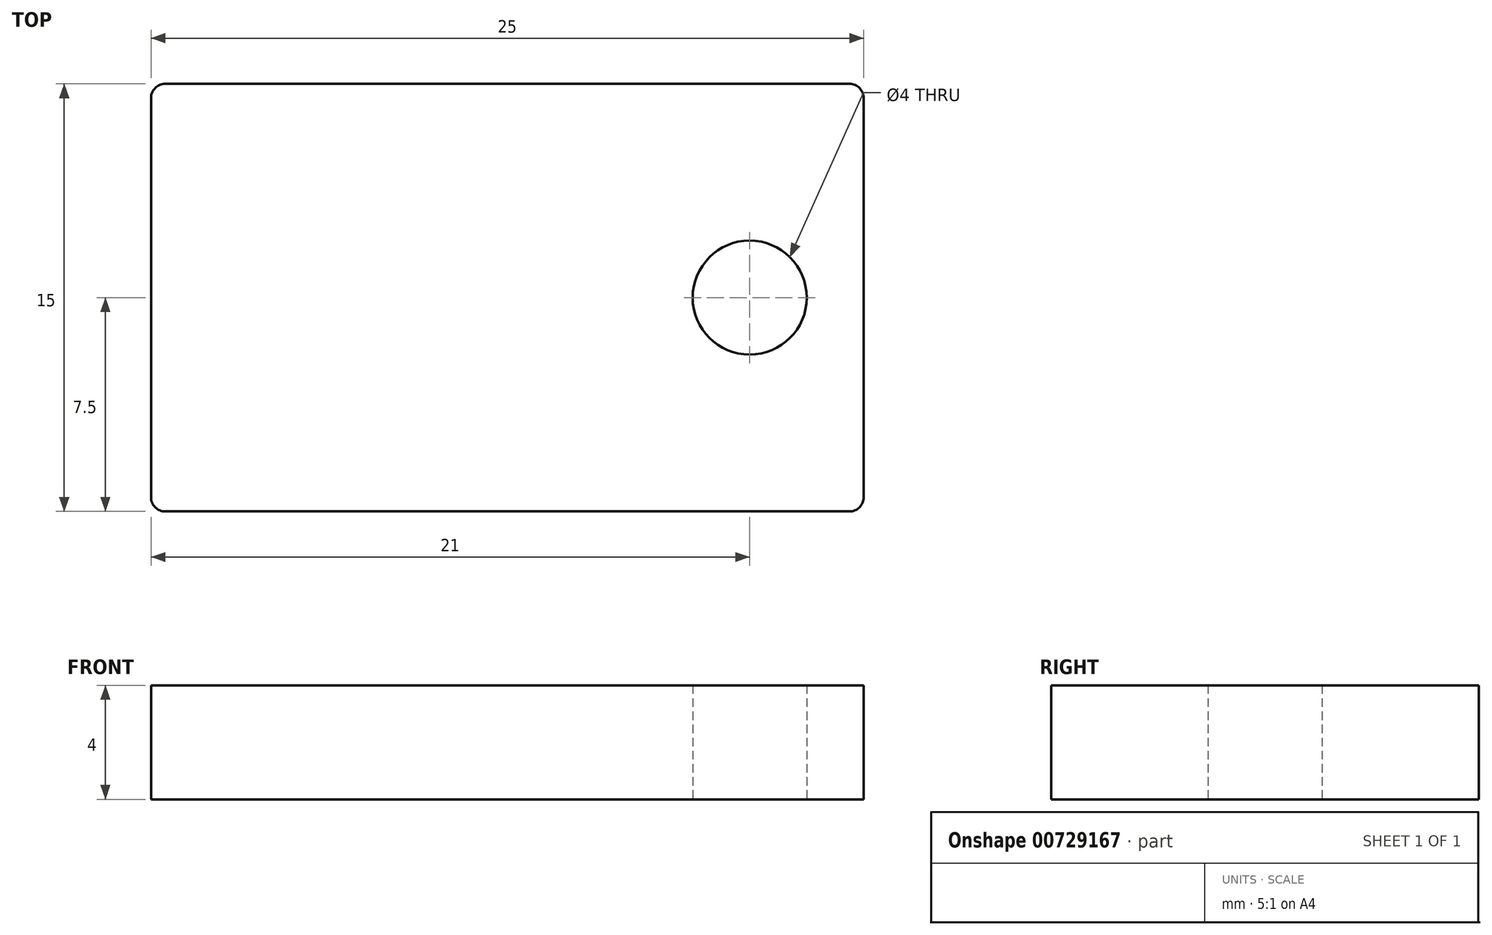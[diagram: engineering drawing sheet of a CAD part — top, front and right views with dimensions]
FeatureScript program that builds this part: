
annotation { "Feature Type Name" : "Feature", "Feature Type Description" : "" }
export const myFeature = defineFeature(function(context is Context, id is Id, definition is map)
    precondition{}
    {
        {
            var Q0;
            Q0=qCreatedBy(makeId("Top.planeOp"),FACE);
            var sketch = newSketch(context, id + "F0", { "sketchPlane" : qUnion([Q0])});
            skLineSegment(sketch, "E0.bottom", {"start": v(12, -7.5) * mm, "end": v(-12, -7.5) * mm});
            skLineSegment(sketch, "E0.top", {"start": v(12, 7.5) * mm, "end": v(-12, 7.5) * mm});
            skLineSegment(sketch, "E0.left", {"start": v(12.5, -7) * mm, "end": v(12.5, 7) * mm});
            skLineSegment(sketch, "E0.right", {"start": v(-12.5, -7) * mm, "end": v(-12.5, 7) * mm});
            skPoint(sketch, "E0.middle", {"position": v(0, 0) * mm});
            skCircle(sketch, "E1", {"center": v(8.5, 0) * mm, "radius": 2 * mm});
            skPoint(sketch, "E1.centerSnap0", {"position": v(12.5, 0) * mm});
            skPoint(sketch, "E2.visualSharp", {"position": v(-12.5, 7.5) * mm});
            skArc(sketch, "E2.filletArc", {"start": v(-12, 7.5) * mm, "mid": v(-12.35, 7.35) * mm, "end": v(-12.5, 7) * mm});
            skPoint(sketch, "E3.visualSharp", {"position": v(-12.5, -7.5) * mm});
            skArc(sketch, "E3.filletArc", {"start": v(-12.5, -7) * mm, "mid": v(-12.35, -7.35) * mm, "end": v(-12, -7.5) * mm});
            skPoint(sketch, "E4.visualSharp", {"position": v(12.5, 7.5) * mm});
            skArc(sketch, "E4.filletArc", {"start": v(12.5, 7) * mm, "mid": v(12.35, 7.35) * mm, "end": v(12, 7.5) * mm});
            skPoint(sketch, "E5.visualSharp", {"position": v(12.5, -7.5) * mm});
            skArc(sketch, "E5.filletArc", {"start": v(12, -7.5) * mm, "mid": v(12.35, -7.35) * mm, "end": v(12.5, -7) * mm});
            skSolve(sketch);
        }
        {
            var Q0;
            Q0 = qSketchRegion(id + "F0", true);
            extrude(context, id + "F1", {"entities" : qUnion([Q0]), "depth" : 4 * mm, "offsetDistance" : 25 * mm});
        }
    });
